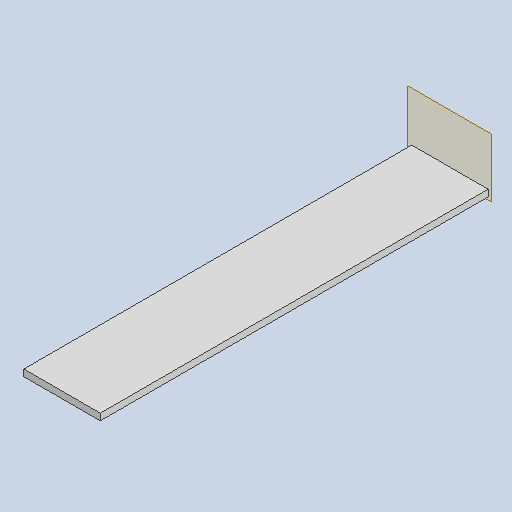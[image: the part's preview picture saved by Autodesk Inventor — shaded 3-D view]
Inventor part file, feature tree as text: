
AUTODESK INVENTOR PART (.ipt)
format: ipt  version: 2023 (Build 270158030, 158C)  size: 147,456 bytes
history: native  units: mm
features: other x4, reference x3, plane x1, extrude x1, sketch x1
ambient origin geometry x8: Origin, YZ Plane, XZ Plane, XY Plane, X Axis, Y Axis, Z Axis, Center Point
bodies: Body1 (feature_tree)
feature tree (10):
  other  "back-plane"
  plane  "Work Plane1"
  extrude  "Extrusion1"  [1 undecoded]
  sketch  "Sketch1"  dims[d0=2030.0mm d1=0.0mm]
  reference  "Reference1"
  reference  "Reference2"
  reference  "Reference3"
  other  "<userpath>\Documents\0004-inventor\3D-CAD-main\primary-engineer-bench.iam"
  other  "primary-engineer-bench.iam"
  other  "bench-end-peice:1"
note: 1 required parameter value undecoded (feature->parameter linkage not recoverable at this tier; creation-order binding heuristic only, values carry confidence <= 0.55)
